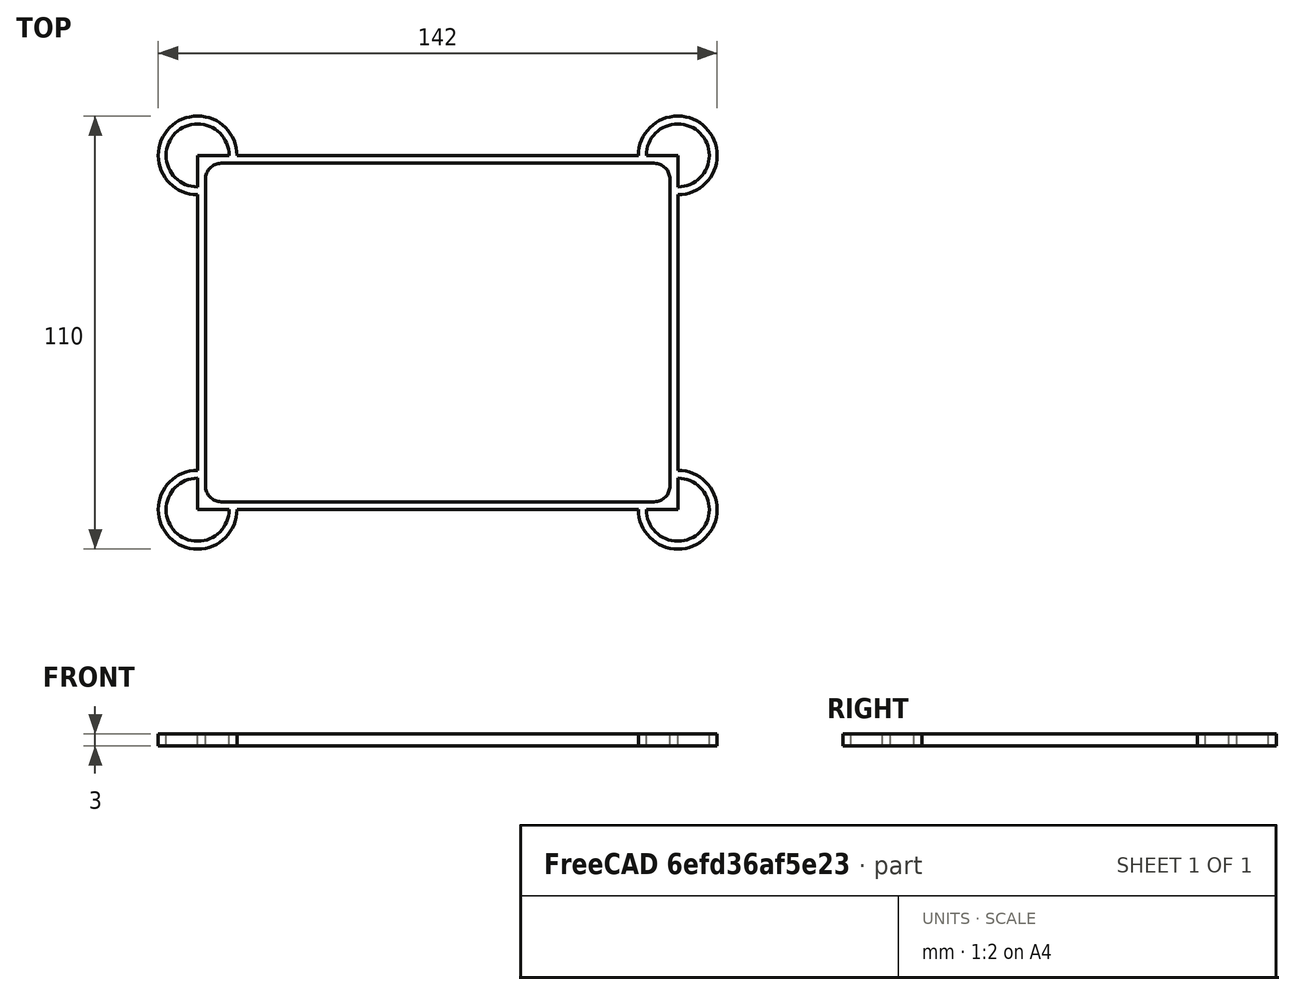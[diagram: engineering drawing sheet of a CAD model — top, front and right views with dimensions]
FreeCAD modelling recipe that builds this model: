
FCSTD DOCUMENT  (FreeCAD 0.18.4R)
Label: PrintFrameMidBox
License: All rights reserved
LicenseURL: http://en.wikipedia.org/wiki/All_rights_reserved
objects: Part::Box×8, Part::Cylinder×8, Part::MultiFuse×6, Part::Cut×4, Part::Fillet×1, Mesh::Feature×1
note: 27 computed .brp shape members not serialized (recipe doc carries the construction recipe); baked Part::Feature solids carry a one-line shape summary decoded from their .brp

FEATURE [Part::Box] Box  label="Würfel001"
  AttacherType = Attacher::AttachEngine3D
  Height = 3
  Length = 118
  Width = 2
FEATURE [Part::Box] Box001  label="Würfel002"
  AttacherType = Attacher::AttachEngine3D
  Height = 3
  Length = 118
  Placement = pos=(0,88,0) rot=(0,0,1;0rad)
  Width = 2
FEATURE [Part::Box] Box002  label="Würfel003"
  AttacherType = Attacher::AttachEngine3D
  Height = 3
  Length = 2
  Placement = pos=(-2,0,0) rot=(0,0,1;0rad)
  Width = 90
FEATURE [Part::Box] Box003  label="Würfel004"
  AttacherType = Attacher::AttachEngine3D
  Height = 3
  Length = 2
  Placement = pos=(118,0,0) rot=(0,0,1;0rad)
  Width = 90
FEATURE [Part::MultiFuse] Fusion  label="Rahmen"
  Shapes = -> [Box,Box002,Box001,Box003]
FEATURE [Part::Cylinder] Cylinder  label="Zylinder002"
  Angle = 360
  AttacherType = Attacher::AttachEngine3D
  Height = 5
  Placement = pos=(-2,0,-1) rot=(0,0,1;0rad)
  Radius = 8
FEATURE [Part::Cylinder] Cylinder001  label="Zylinder001"
  Angle = 360
  AttacherType = Attacher::AttachEngine3D
  Height = 3
  Placement = pos=(-2,0,0) rot=(0,0,1;0rad)
  Radius = 10
FEATURE [Part::Box] Box004  label="Würfel"
  AttacherType = Attacher::AttachEngine3D
  Height = 5
  Length = 10
  Placement = pos=(-2,0,-1) rot=(0,0,1;0rad)
  Width = 10
FEATURE [Part::MultiFuse] Fusion001
  Shapes = -> [Cylinder,Box004]
FEATURE [Part::Cut] Cut  label="Ecke001"
  Base = -> Cylinder001
  Tool = -> Fusion001
FEATURE [Part::Cylinder] Cylinder002  label="Zylinder003"
  Angle = 360
  AttacherType = Attacher::AttachEngine3D
  Height = 3
  Placement = pos=(-2,0,0) rot=(0,0,1;0rad)
  Radius = 10
FEATURE [Part::Box] Box005  label="Würfel005"
  AttacherType = Attacher::AttachEngine3D
  Height = 5
  Length = 10
  Placement = pos=(-2,0,-1) rot=(0,0,1;0rad)
  Width = 10
FEATURE [Part::Cylinder] Cylinder003  label="Zylinder004"
  Angle = 360
  AttacherType = Attacher::AttachEngine3D
  Height = 5
  Placement = pos=(-2,0,-1) rot=(0,0,1;0rad)
  Radius = 8
FEATURE [Part::MultiFuse] Fusion002
  Shapes = -> [Cylinder003,Box005]
FEATURE [Part::Cut] Cut001  label="Ecke002"
  Base = -> Cylinder002
  Placement = pos=(-2,88,0) rot=(0,0,-1;1.5708rad)
  Tool = -> Fusion002
FEATURE [Part::Cylinder] Cylinder004  label="Zylinder005"
  Angle = 360
  AttacherType = Attacher::AttachEngine3D
  Height = 3
  Placement = pos=(-2,0,0) rot=(0,0,1;0rad)
  Radius = 10
FEATURE [Part::Box] Box006  label="Würfel006"
  AttacherType = Attacher::AttachEngine3D
  Height = 5
  Length = 10
  Placement = pos=(-2,0,-1) rot=(0,0,1;0rad)
  Width = 10
FEATURE [Part::Cylinder] Cylinder005  label="Zylinder006"
  Angle = 360
  AttacherType = Attacher::AttachEngine3D
  Height = 5
  Placement = pos=(-2,0,-1) rot=(0,0,1;0rad)
  Radius = 8
FEATURE [Part::MultiFuse] Fusion003
  Shapes = -> [Cylinder005,Box006]
FEATURE [Part::Cut] Cut002  label="Ecke003"
  Base = -> Cylinder004
  Placement = pos=(120,2,0) rot=(0,0,1;1.5708rad)
  Tool = -> Fusion003
FEATURE [Part::Cylinder] Cylinder006  label="Zylinder007"
  Angle = 360
  AttacherType = Attacher::AttachEngine3D
  Height = 3
  Placement = pos=(-2,0,0) rot=(0,0,1;0rad)
  Radius = 10
FEATURE [Part::Box] Box007  label="Würfel007"
  AttacherType = Attacher::AttachEngine3D
  Height = 5
  Length = 10
  Placement = pos=(-2,0,-1) rot=(0,0,1;0rad)
  Width = 10
FEATURE [Part::Cylinder] Cylinder007  label="Zylinder008"
  Angle = 360
  AttacherType = Attacher::AttachEngine3D
  Height = 5
  Placement = pos=(-2,0,-1) rot=(0,0,1;0rad)
  Radius = 8
FEATURE [Part::MultiFuse] Fusion004
  Shapes = -> [Cylinder007,Box007]
FEATURE [Part::Cut] Cut003  label="Ecke004"
  Base = -> Cylinder006
  Placement = pos=(118,90,0) rot=(0,0,1;3.14159rad)
  Tool = -> Fusion004
FEATURE [Part::MultiFuse] Fusion005
  Shapes = -> [Cut003,Fusion,Cut002,Cut,Cut001]
FEATURE [Part::Fillet] Fillet
  Base = -> Fusion005
  Edges = 4 edges r=4: [Edge33,Edge34,Edge79,Edge85]
FEATURE [Mesh::Feature] Mesh  label="Fillet (Meshed)"
